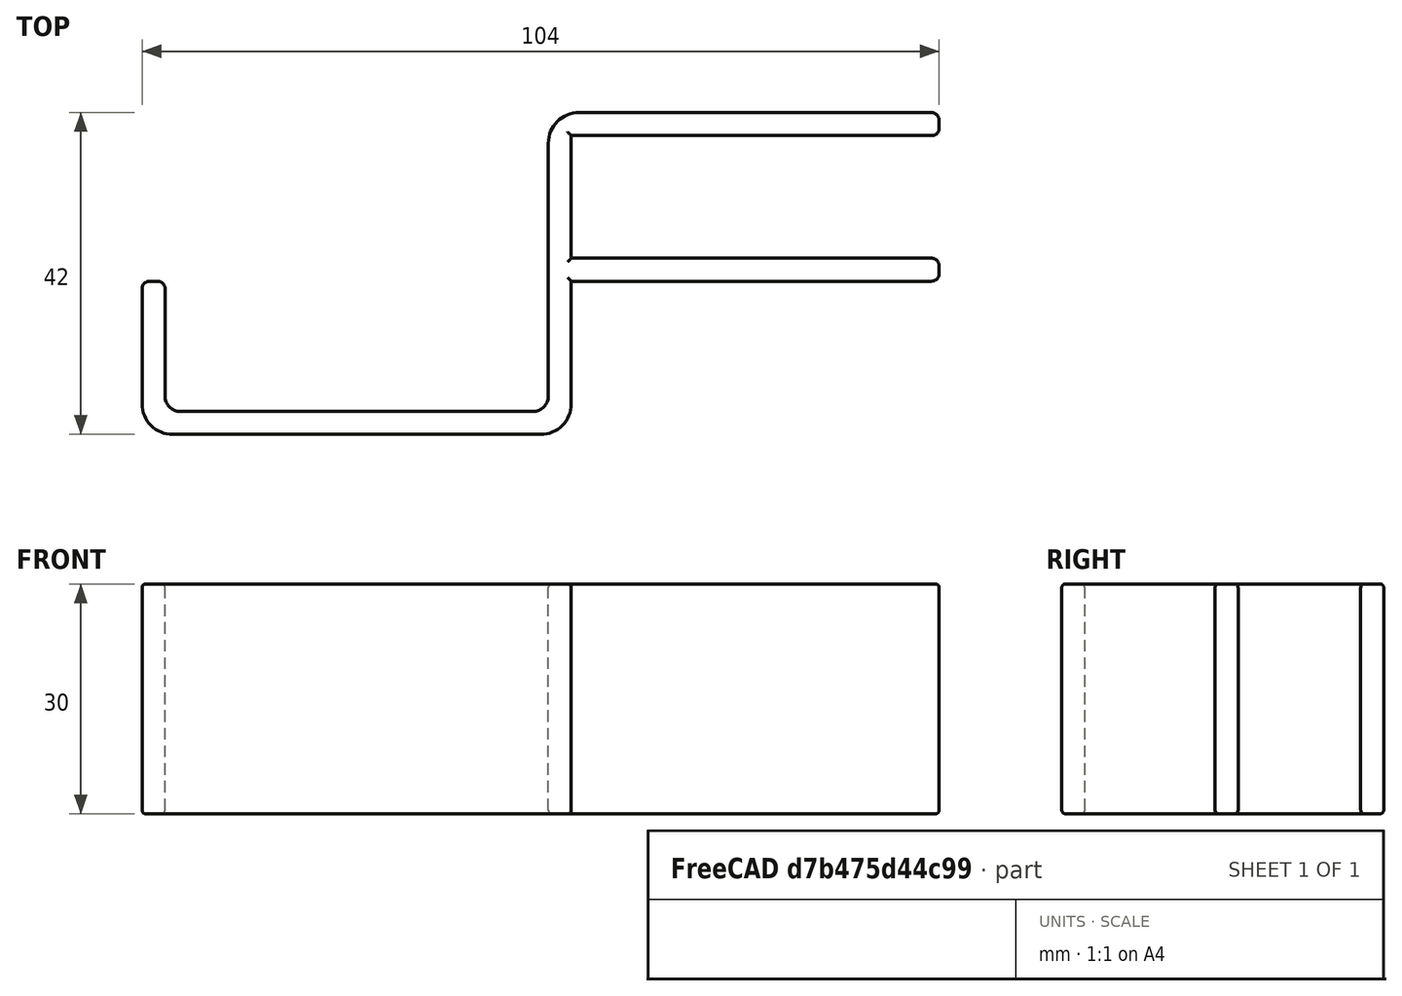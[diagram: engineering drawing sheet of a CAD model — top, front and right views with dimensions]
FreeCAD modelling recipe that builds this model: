
FCSTD DOCUMENT  (FreeCAD 0.21R)
Label: cedric
License: All rights reserved
LicenseURL: http://en.wikipedia.org/wiki/All_rights_reserved
objects: Sketcher::SketchObject×1, PartDesign::Pad×1, PartDesign::Fillet×1, PartDesign::Body×1
note: 6 computed .brp shape members not serialized (recipe doc carries the construction recipe); baked Part::Feature solids carry a one-line shape summary decoded from their .brp

FEATURE [Sketcher::SketchObject] Sketch
  FullyConstrained = false
  Placement = pos=(0,0,0) rot=(0,0,1;3.14159rad)
  sketch-geometry (25):
    g0: ArcOfCircle CenterX=1 CenterY=19 CenterZ=0 NormalX=0 NormalY=0 NormalZ=1 AngleXU=3.14159 Radius=4 StartAngle=4.71239 EndAngle=6.28319
    g1: ArcOfCircle CenterX=-4 CenterY=-15 CenterZ=0 NormalX=0 NormalY=0 NormalZ=1 AngleXU=3.14159 Radius=4 StartAngle=1.5708 EndAngle=3.14159
    g2: LineSegment StartX=-3 StartY=-16 StartZ=0 EndX=-3 EndY=0 EndZ=0
    g3: LineSegment StartX=1 StartY=23 StartZ=0 EndX=49 EndY=23 EndZ=0
    g4: ArcOfCircle CenterX=49 CenterY=19 CenterZ=0 NormalX=0 NormalY=0 NormalZ=1 AngleXU=3.14159 Radius=4 StartAngle=3.14159 EndAngle=4.71239
    g5: ArcOfCircle CenterX=48 CenterY=18 CenterZ=0 NormalX=0 NormalY=0 NormalZ=1 AngleXU=3.14159 Radius=2 StartAngle=3.14159 EndAngle=4.71239
    g6: LineSegment StartX=2 StartY=20 StartZ=0 EndX=48 EndY=20 EndZ=0
    g7: LineSegment StartX=-2.7e-15 StartY=-15 StartZ=0 EndX=3.3e-15 EndY=18 EndZ=0
    g8: ArcOfCircle CenterX=2 CenterY=18 CenterZ=0 NormalX=0 NormalY=0 NormalZ=1 AngleXU=3.14159 Radius=2 StartAngle=4.71239 EndAngle=6.28319
    g9: LineSegment StartX=53 StartY=19 StartZ=0 EndX=53 EndY=4 EndZ=0
    g10: ArcOfCircle CenterX=52 CenterY=4 CenterZ=0 NormalX=0 NormalY=0 NormalZ=1 AngleXU=3.14159 Radius=1 StartAngle=1.5708 EndAngle=3.14159
    g11: LineSegment StartX=52 StartY=3 StartZ=0 EndX=51 EndY=3 EndZ=0
    g12: LineSegment StartX=50 StartY=18 StartZ=0 EndX=50 EndY=4 EndZ=0
    g13: ArcOfCircle CenterX=51 CenterY=4 CenterZ=0 NormalX=0 NormalY=0 NormalZ=1 AngleXU=3.14159 Radius=1 StartAngle=0 EndAngle=1.5708
    g14: ArcOfCircle CenterX=-50 CenterY=1 CenterZ=0 NormalX=0 NormalY=0 NormalZ=1 AngleXU=3.14159 Radius=1 StartAngle=0 EndAngle=1.5708
    g15: LineSegment StartX=-51 StartY=1 StartZ=0 EndX=-51 EndY=2 EndZ=0
    g16: ArcOfCircle CenterX=-50 CenterY=2 CenterZ=0 NormalX=0 NormalY=0 NormalZ=1 AngleXU=3.14159 Radius=1 StartAngle=4.71239 EndAngle=6.28319
    g17: ArcOfCircle CenterX=-50 CenterY=-18 CenterZ=0 NormalX=0 NormalY=0 NormalZ=1 AngleXU=3.14159 Radius=1 StartAngle=0 EndAngle=1.5708
    g18: LineSegment StartX=-51 StartY=-18 StartZ=0 EndX=-51 EndY=-17 EndZ=0
    g19: ArcOfCircle CenterX=-50 CenterY=-17 CenterZ=0 NormalX=0 NormalY=0 NormalZ=1 AngleXU=3.14159 Radius=1 StartAngle=4.71239 EndAngle=6.28319
    g20: LineSegment StartX=-4 StartY=-19 StartZ=0 EndX=-50 EndY=-19 EndZ=0
    g21: LineSegment StartX=-3 StartY=-16 StartZ=0 EndX=-50 EndY=-16 EndZ=0
    g22: LineSegment StartX=-3 StartY=0 StartZ=0 EndX=-50 EndY=6.2e-15 EndZ=0
    g23: LineSegment StartX=-3 StartY=3 StartZ=0 EndX=-3 EndY=19 EndZ=0
    g24: LineSegment StartX=-3 StartY=3 StartZ=0 EndX=-50 EndY=3 EndZ=0
  constraints (25):
    c: Coincident(g17,g18)
    c: Coincident(g18,g19)
    c: Coincident(g14,g15)
    c: Coincident(g15,g16)
    c: Coincident(g17,g20)
    c: Coincident(g19,g21)
    c: Coincident(g14,g22)
    c: Coincident(g16,g24)
    c: Coincident(g1,g20)
    c: Coincident(g2,g21)
    c: Coincident(g2,g22)
    c: Coincident(g23,g24)
    c: Coincident(g0,g23)
    c: Coincident(g1,g7)
    c: Coincident(g7,g8)
    c: Coincident(g0,g3)
    c: Coincident(g6,g8)
    c: Coincident(g5,g6)
    c: Coincident(g3,g4)
    c: Coincident(g12,g13)
    c: Coincident(g5,g12)
    c: Coincident(g11,g13)
    c: Coincident(g10,g11)
    c: Coincident(g9,g10)
    c: Coincident(g4,g9)
FEATURE [PartDesign::Pad] Pad
  Direction = (0,0,1)
  Length = 30
  Length2 = 10
  Placement = pos=(0,0,0) rot=(0,0,1;3.14159rad)
  Profile = -> Sketch
  ReferenceAxis = -> Sketch [N_Axis]
  Type = 0
FEATURE [PartDesign::Fillet] Fillet
  Base = -> Pad [Face26,Face27]
  BaseFeature = -> Pad
  Placement = pos=(0,0,0) rot=(0,0,1;3.14159rad)
  Radius = 0.5
  SupportTransform = false
  UseAllEdges = false
FEATURE [PartDesign::Body] Body  label="Corps"
  Group = -> [Sketch,Pad,Fillet]
  Origin = -> Origin
  Tip = -> Fillet
